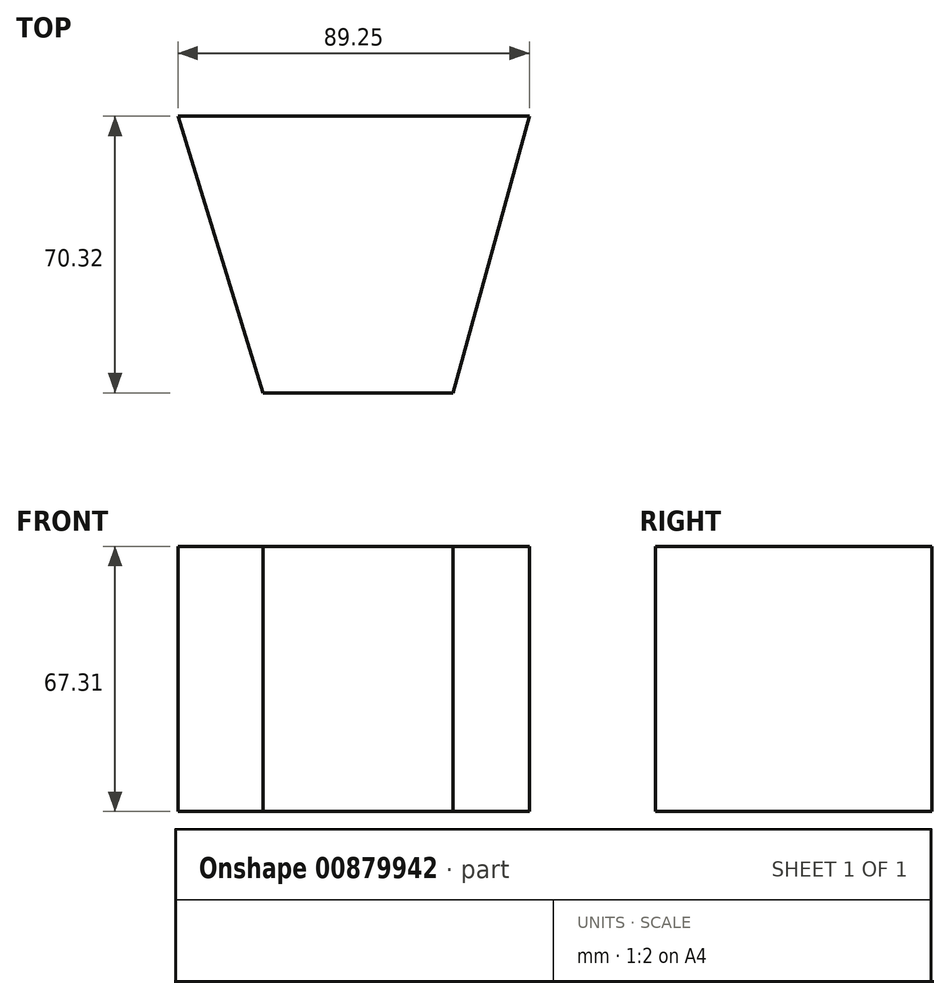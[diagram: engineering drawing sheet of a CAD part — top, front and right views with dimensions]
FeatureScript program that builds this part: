
annotation { "Feature Type Name" : "Feature", "Feature Type Description" : "" }
export const myFeature = defineFeature(function(context is Context, id is Id, definition is map)
    precondition{}
    {
        {
            var Q0;
            Q0=qCreatedBy(makeId("Top.planeOp"),FACE);
            var sketch = newSketch(context, id + "F0", { "sketchPlane" : qUnion([Q0])});
            skLineSegment(sketch, "E0.bottom", {"start": v(-43.96, 25.47) * mm, "end": v(45.3, 25.47) * mm});
            skLineSegment(sketch, "E0.top", {"start": v(-22.38, -44.85) * mm, "end": v(25.9, -44.85) * mm});
            skLineSegment(sketch, "E0.left", {"start": v(-43.96, 25.47) * mm, "end": v(-22.38, -44.85) * mm});
            skLineSegment(sketch, "E0.right", {"start": v(45.3, 25.47) * mm, "end": v(25.9, -44.85) * mm});
            skSolve(sketch);
        }
        {
            var Q0;
            Q0=makeQuery(id+"F0.imprint","IMPRINT",FACE,{"disambiguationData":[TD([[makeQuery(id+"F0.imprint","IMPRINT",EDGE,{"derivedFrom":sQuery(id+"F0.wireOp",EDGE,"E0.bottom")}),-1.0]])]});
            extrude(context, id + "F1", {"entities" : qUnion([Q0]), "depth" : 67.3 * mm, "offsetDistance" : 25.4 * mm});
        }
    });
